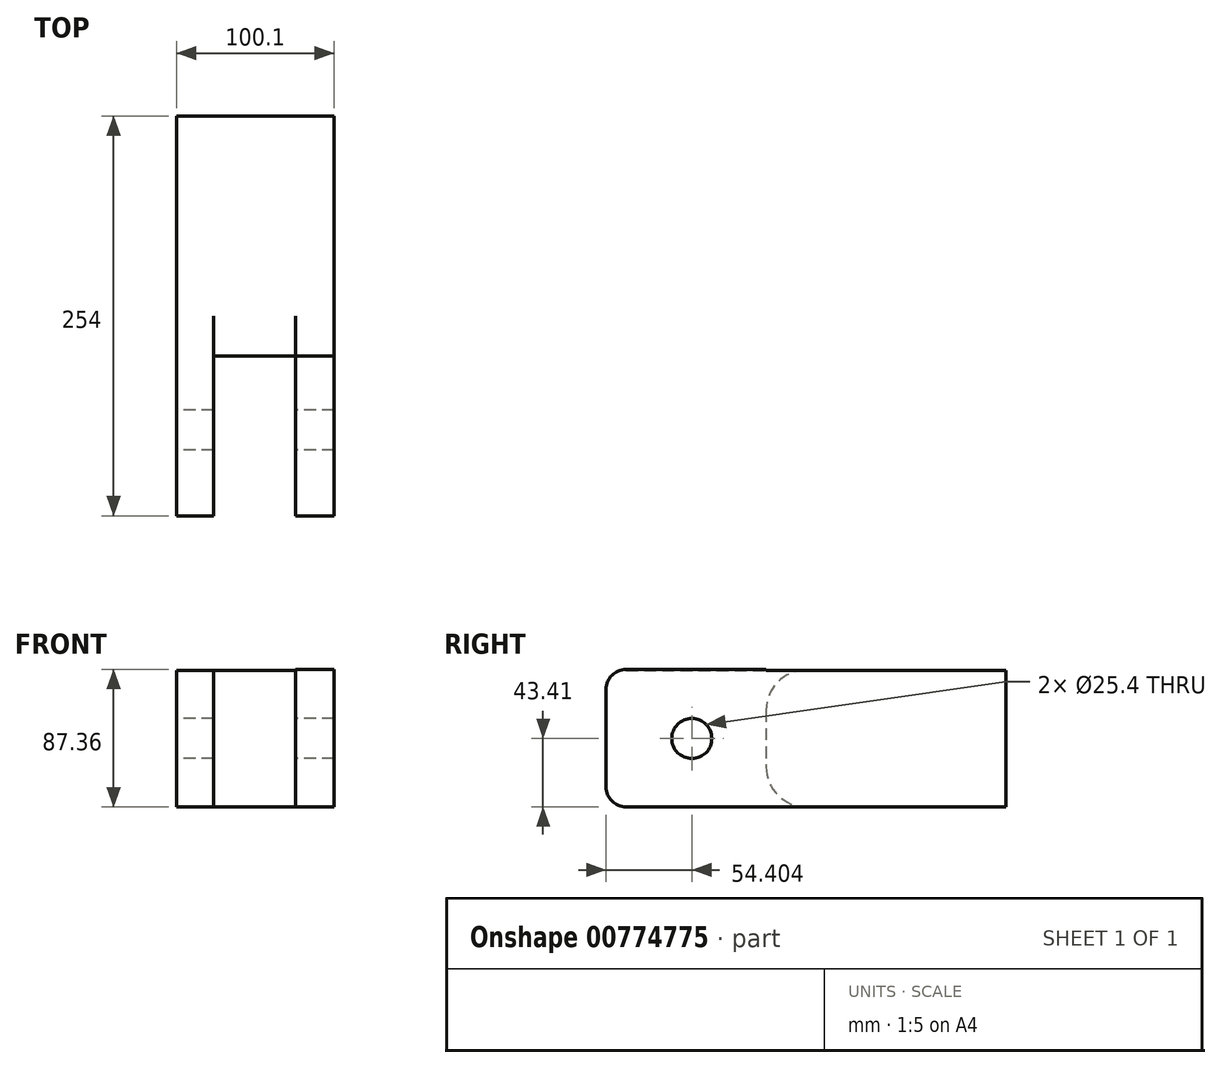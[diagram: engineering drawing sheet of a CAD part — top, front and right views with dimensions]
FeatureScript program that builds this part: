
annotation { "Feature Type Name" : "Feature", "Feature Type Description" : "" }
export const myFeature = defineFeature(function(context is Context, id is Id, definition is map)
    precondition{}
    {
        {
            var Q0;
            Q0=qCreatedBy(makeId("Front.planeOp"),FACE);
            var sketch = newSketch(context, id + "F0", { "sketchPlane" : qUnion([Q0])});
            skLineSegment(sketch, "E0.bottom", {"start": v(50.05, 43.4) * mm, "end": v(-50.05, 43.4) * mm});
            skLineSegment(sketch, "E0.top", {"start": v(50.05, -43.4) * mm, "end": v(-50.05, -43.4) * mm});
            skLineSegment(sketch, "E0.left", {"start": v(50.05, 43.4) * mm, "end": v(50.05, -43.4) * mm});
            skLineSegment(sketch, "E0.right", {"start": v(-50.05, 43.4) * mm, "end": v(-50.05, -43.4) * mm});
            skPoint(sketch, "E0.middle", {"position": v(0, 0) * mm});
            skSolve(sketch);
        }
        {
            var Q0;
            Q0 = qSketchRegion(id + "F0", true);
            extrude(context, id + "F1", {"entities" : qUnion([Q0]), "depth" : 152.4 * mm, "offsetDistance" : 25.4 * mm});
        }
        {
            var Q0;
            Q0=makeQuery(id+"F1.opExtrude","CAP_FACE",FACE,{"disambiguationData":[OSD([sQuery(id+"F0.wireOp",EDGE,"E0.bottom"),sQuery(id+"F0.wireOp",EDGE,"E0.top"),sQuery(id+"F0.wireOp",EDGE,"E0.left"),sQuery(id+"F0.wireOp",EDGE,"E0.right")])],"isStart":false});
            var sketch = newSketch(context, id + "F2", { "sketchPlane" : qUnion([Q0])});
            skLineSegment(sketch, "E1.bottom", {"start": v(-50.05, 43.4) * mm, "end": v(-26.56, 43.4) * mm});
            skLineSegment(sketch, "E1.top", {"start": v(-50.05, -43.4) * mm, "end": v(-26.56, -43.4) * mm});
            skLineSegment(sketch, "E1.left", {"start": v(-50.05, 43.4) * mm, "end": v(-50.05, -43.4) * mm});
            skLineSegment(sketch, "E1.right", {"start": v(-26.56, 43.4) * mm, "end": v(-26.56, -43.4) * mm});
            skLineSegment(sketch, "E2.bottom", {"start": v(-26.56, 43.4) * mm, "end": v(26.33, 43.4) * mm});
            skLineSegment(sketch, "E2.top", {"start": v(-26.56, -43.4) * mm, "end": v(26.33, -43.4) * mm});
            skLineSegment(sketch, "E2.right", {"start": v(26.33, 43.4) * mm, "end": v(26.33, -43.4) * mm});
            skLineSegment(sketch, "E3.bottom", {"start": v(25.66, 43.95) * mm, "end": v(50.05, 43.95) * mm});
            skLineSegment(sketch, "E3.top", {"start": v(25.66, -43.4) * mm, "end": v(50.05, -43.4) * mm});
            skLineSegment(sketch, "E3.left", {"start": v(25.66, 43.95) * mm, "end": v(25.66, -43.4) * mm});
            skLineSegment(sketch, "E3.right", {"start": v(50.05, 43.95) * mm, "end": v(50.05, -43.4) * mm});
            skSolve(sketch);
        }
        {
            var Q0;
            Q0=makeQuery(id+"F2.imprint","IMPRINT",FACE,{"disambiguationData":[TD([[makeQuery(id+"F2.imprint","IMPRINT",EDGE,{"derivedFrom":sQuery(id+"F2.wireOp",EDGE,"E1.bottom")}),1.0]])]});
            var Q1;
            {var subQ3=sQuery(id+"F2.wireOp",EDGE,"E3.bottom");Q1=makeQuery(id+"F2.imprint","IMPRINT",FACE,{"disambiguationData":[TD([[makeQuery(id+"F2.imprint","IMPRINT",EDGE,{"derivedFrom":subQ3}),-1.0]])]});}
            var Q2;
            {var subQ0=sQuery(id+"F2.wireOp",EDGE,"E2.right");Q2=makeQuery(id+"F2.imprint","IMPRINT",FACE,{"disambiguationData":[TD([[makeQuery(id+"F2.imprint","IMPRINT",EDGE,{"derivedFrom":subQ0}),-1.0]])]});}
            var Q3;
            {var subQ0=sQuery(id+"F2.wireOp",EDGE,"E2.right");Q3=makeQuery(id+"F2.imprint","IMPRINT",FACE,{"disambiguationData":[TD([[makeQuery(id+"F2.imprint","IMPRINT",EDGE,{"derivedFrom":subQ0}),1.0]])]});}
            extrude(context, id + "F3", {"entities" : qUnion([Q0, Q1, Q2, Q3]), "operationType" : NewBodyOperationType.ADD, "depth" : 101.6 * mm, "offsetDistance" : 25.4 * mm});
        }
        {
            var Q0;
            Q0=makeQuery(id+"F3.opExtrude","CAP_EDGE",EDGE,{"disambiguationData":[OSD([sQuery(id+"F2.wireOp",EDGE,"E1.top")])],"isStart":false});
            var Q1;
            Q1=makeQuery(id+"F3.opExtrude","CAP_EDGE",EDGE,{"disambiguationData":[OSD([sQuery(id+"F2.wireOp",EDGE,"E3.top")])],"isStart":false});
            var Q2;
            Q2=makeQuery(id+"F3.opExtrude","CAP_EDGE",EDGE,{"disambiguationData":[OSD([sQuery(id+"F2.wireOp",EDGE,"E3.bottom")])],"isStart":false});
            var Q3;
            Q3=makeQuery(id+"F3.opExtrude","CAP_EDGE",EDGE,{"disambiguationData":[OSD([sQuery(id+"F2.wireOp",EDGE,"E1.bottom")])],"isStart":false});
            fillet(context, id + "F4", {"entities" : qUnion([Q0, Q1, Q2, Q3]), "radius" : 12.7 * mm, "tangentPropagation" : true, "allowEdgeOverflow" : false});
        }
        {
            var Q0;
            Q0=makeQuery(id+"F3.boolean.opBoolean","MERGE",FACE,{"derivedFrom":[makeQuery(id+"F1.opExtrude","SWEPT_FACE",FACE,{"disambiguationData":[OSD([sQuery(id+"F0.wireOp",EDGE,"E0.right")])]}),makeQuery(id+"F3.opExtrude","SWEPT_FACE",FACE,{"disambiguationData":[OSD([sQuery(id+"F2.wireOp",EDGE,"E1.left")])]})]});
            var sketch = newSketch(context, id + "F5", { "sketchPlane" : qUnion([Q0])});
            skCircle(sketch, "E4", {"center": v(199.6, 0) * mm, "radius": 27.71 * mm});
            skSolve(sketch);
        }
        {
            var Q0;
            Q0=sQuery(id+"F5.wireOp",VERTEX,"E4.center");
            var Q1;
            Q1=makeQuery(id+"F1.opExtrude","SWEPT_BODY",BODY,{"disambiguationData":[OSD([sQuery(id+"F0.wireOp",EDGE,"E0.bottom"),sQuery(id+"F0.wireOp",EDGE,"E0.top"),sQuery(id+"F0.wireOp",EDGE,"E0.left"),sQuery(id+"F0.wireOp",EDGE,"E0.right")])]});
            hole(context, id + "F6", {"style" : HoleStyle.SIMPLE, "endStyle" : HoleEndStyle.THROUGH, "holeDiameter" : 25.4 * mm, "majorDiameter" : 6.35 * mm, "isTappedThrough" : true, "tappedDepth" : 12.7 * mm, "tapClearance" : 3, "locations" : qUnion([Q0]), "scope" : qUnion([Q1])});
        }
        {
            var Q0;
            Q0=makeQuery(id+"F1.opExtrude","CAP_EDGE",EDGE,{"disambiguationData":[OSD([sQuery(id+"F0.wireOp",EDGE,"E0.top")])],"isStart":false});
            var Q1;
            {var subQ0=sQuery(id+"F0.wireOp",EDGE,"E0.bottom");Q1=makeQuery(id+"F3.boolean.opBoolean","SPLIT",EDGE,{"disambiguationData":[topologyDisambiguationEdgeConnected([makeQuery(id+"F1.opExtrude","CAP_FACE",FACE,{"disambiguationData":[OSD([subQ0,sQuery(id+"F0.wireOp",EDGE,"E0.top"),sQuery(id+"F0.wireOp",EDGE,"E0.left"),sQuery(id+"F0.wireOp",EDGE,"E0.right")])],"isStart":false})])],"derivedFrom":makeQuery(id+"F1.opExtrude","CAP_EDGE",EDGE,{"disambiguationData":[OSD([subQ0])],"isStart":false})});}
            fillet(context, id + "F7", {"entities" : qUnion([Q0, Q1]), "radius" : 25.4 * mm, "tangentPropagation" : true, "allowEdgeOverflow" : false});
        }
    });
